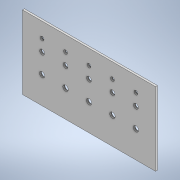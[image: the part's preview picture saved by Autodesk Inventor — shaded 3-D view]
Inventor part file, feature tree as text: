
AUTODESK INVENTOR PART (.ipt)
format: ipt  version: 2021 (Build 250183000, 183)  size: 154,112 bytes
history: native  units: in
note: dims shown in document units (in); Inventor stores cm internally (conversion verified against a paired STEP export)
features: extrude x2, sketch x2
ambient origin geometry x8: Origin, YZ Plane, XZ Plane, XY Plane, X Axis, Y Axis, Z Axis, Center Point
bodies: Solid1 (feature_tree)
feature tree (4):
  extrude  "Extrusion1"  Depth=0.1in
  extrude  "Extrusion2"  Depth=3.75in
  sketch  "Sketch1"  dims[d2=0.1in d3=0.0in d4=0.2756in]
  sketch  "Sketch2"  dims[d5=0.25in d8=1.0in d9=0.25in d10=0.25in d11=0.25in d12=0.25in d18=0.0in d19=0.0in d20=0.0in d21=0.0in d22=0.1969in d23=0.6in d24=0.0in d25=0.1969in d26=0.1969in d27=0.1969in d28=0.1969in d29=0.6in d34=0.6in d35=0.6in d36=0.6in d37=0.2756in d38=0.2756in d39=0.2756in d40=0.2756in d41=1.2in d42=1.0in d43=1.2in d44=1.0in d45=1.2in d46=1.0in d47=1.2in d48=1.0in d49=1.2in d50=1.2in d51=1.2in d52=1.2in d53=6.8in d55=0.1in d56=0.0in d57=3.75in d58=1.2in d59=1.2in d60=1.2in d61=1.2in d62=0.0in d63=1.0in]
